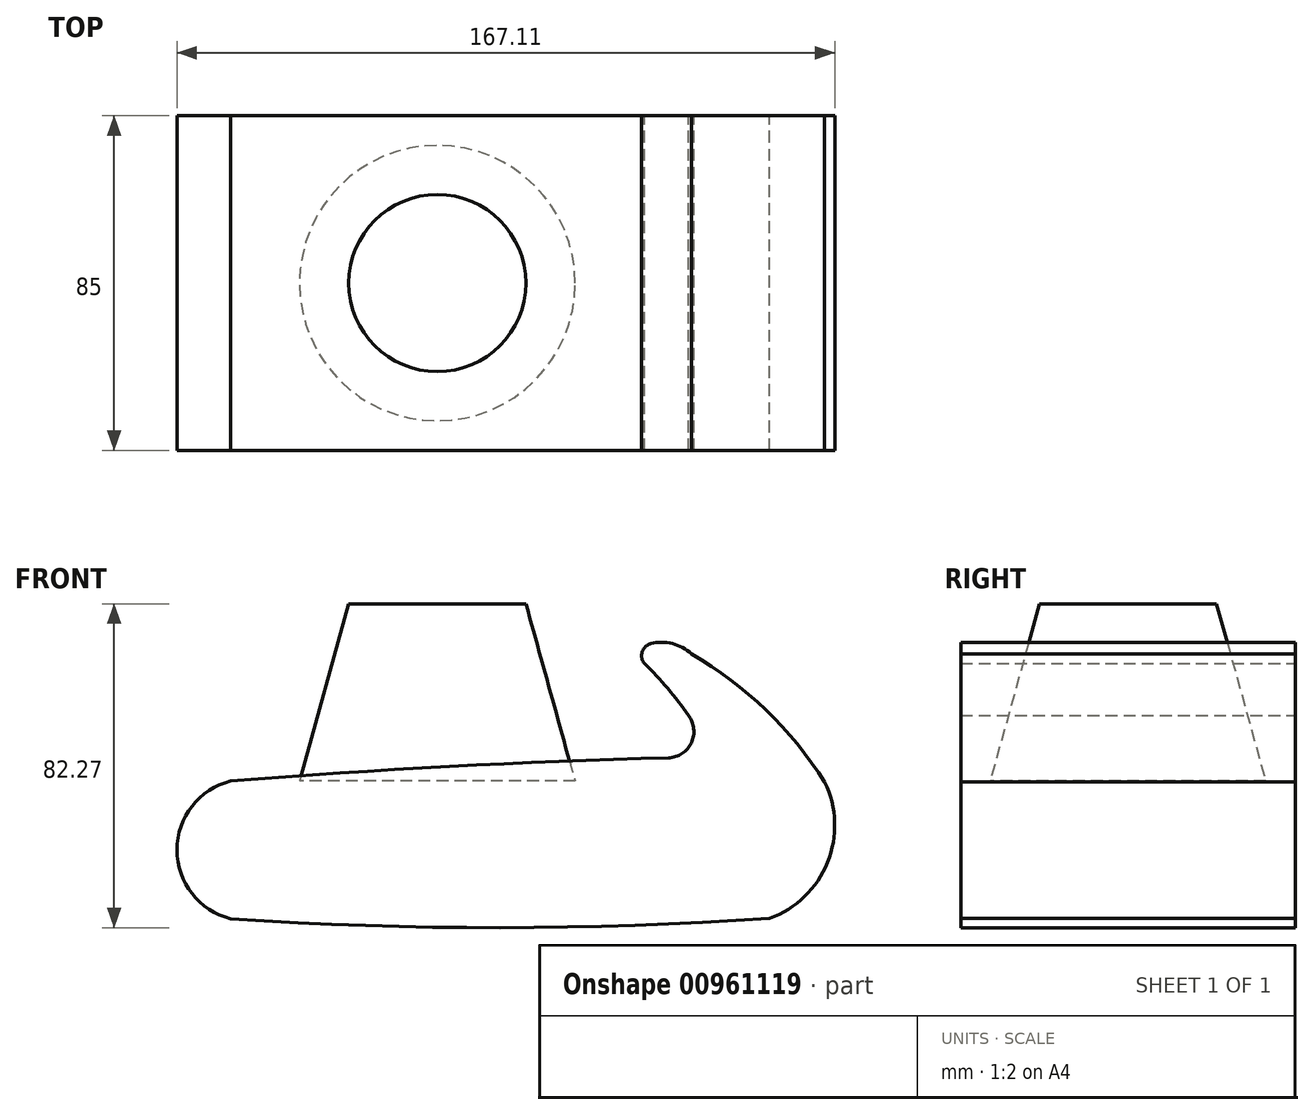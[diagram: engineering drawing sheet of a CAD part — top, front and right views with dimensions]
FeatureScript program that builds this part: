
annotation { "Feature Type Name" : "Feature", "Feature Type Description" : "" }
export const myFeature = defineFeature(function(context is Context, id is Id, definition is map)
    precondition{}
    {
        {
            var Q0;
            Q0=qCreatedBy(makeId("Front.planeOp"),FACE);
            var sketch = newSketch(context, id + "F0", { "sketchPlane" : qUnion([Q0])});
            skLineSegment(sketch, "E0.bottom", {"start": v(52.5, 0) * mm, "end": v(-52.5, 0) * mm, "construction": true});
            skLineSegment(sketch, "E0.top", {"start": v(52.5, 0) * mm, "end": v(-52.5, 0) * mm, "construction": true});
            skLineSegment(sketch, "E0.left", {"start": v(52.5, 0) * mm, "end": v(52.5, 0) * mm});
            skLineSegment(sketch, "E0.right", {"start": v(-52.5, 0) * mm, "end": v(-52.5, 0) * mm});
            skPoint(sketch, "E0.middle", {"position": v(0, 0) * mm});
            skLineSegment(sketch, "E1.bottom", {"start": v(72.5, 0) * mm, "end": v(-72.5, 0) * mm, "construction": true});
            skLineSegment(sketch, "E1.top", {"start": v(72.5, 0) * mm, "end": v(-72.5, 0) * mm, "construction": true});
            skLineSegment(sketch, "E1.left", {"start": v(72.5, 0) * mm, "end": v(72.5, 0) * mm});
            skLineSegment(sketch, "E1.right", {"start": v(-72.5, 0) * mm, "end": v(-72.5, 0) * mm});
            skLineSegment(sketch, "E2.bottom", {"start": v(-52.5, 17.5) * mm, "end": v(-52.5, 17.5) * mm});
            skLineSegment(sketch, "E2.top", {"start": v(-52.5, -17.5) * mm, "end": v(-52.5, -17.5) * mm});
            skLineSegment(sketch, "E2.left", {"start": v(-52.5, 17.5) * mm, "end": v(-52.5, -17.5) * mm, "construction": true});
            skLineSegment(sketch, "E2.right", {"start": v(-52.5, 17.5) * mm, "end": v(-52.5, -17.5) * mm, "construction": true});
            skPoint(sketch, "E2.middle", {"position": v(-52.5, 0) * mm});
            skLineSegment(sketch, "E3.bottom", {"start": v(52.5, 17.5) * mm, "end": v(52.5, 17.5) * mm});
            skLineSegment(sketch, "E3.top", {"start": v(52.5, -17.5) * mm, "end": v(52.5, -17.5) * mm});
            skLineSegment(sketch, "E3.left", {"start": v(52.5, 17.5) * mm, "end": v(52.5, -17.5) * mm, "construction": true});
            skLineSegment(sketch, "E3.right", {"start": v(52.5, 17.5) * mm, "end": v(52.5, -17.5) * mm, "construction": true});
            skPoint(sketch, "E3.middle", {"position": v(52.5, 0) * mm});
            skArc(sketch, "E4", {"start": v(58.7, 23.37) * mm, "mid": v(3.06, 21.19) * mm, "end": v(-52.5, 17.5) * mm});
            skArc(sketch, "E5", {"start": v(58.7, 23.37) * mm, "mid": v(64.55, 27.19) * mm, "end": v(63.77, 34.12) * mm});
            skArc(sketch, "E6", {"start": v(63.77, 34.12) * mm, "mid": v(58.54, 41.01) * mm, "end": v(52.62, 47.31) * mm});
            skArc(sketch, "E7", {"start": v(54.24, 52.38) * mm, "mid": v(52.03, 50.3) * mm, "end": v(52.62, 47.31) * mm});
            skArc(sketch, "E8", {"start": v(64.55, 49.76) * mm, "mid": v(59.74, 52.4) * mm, "end": v(54.24, 52.38) * mm});
            skArc(sketch, "E9", {"start": v(98.4, 17.21) * mm, "mid": v(83.47, 35.56) * mm, "end": v(64.55, 49.76) * mm});
            skArc(sketch, "E10", {"start": v(84.43, -17.4) * mm, "mid": v(99.13, -3.2) * mm, "end": v(98.4, 17.21) * mm});
            skArc(sketch, "E11", {"start": v(-52.5, -17.5) * mm, "mid": v(15.96, -19.77) * mm, "end": v(84.43, -17.4) * mm});
            skArc(sketch, "E12", {"start": v(-52.5, 17.5) * mm, "mid": v(-66.15, 0) * mm, "end": v(-52.5, -17.5) * mm});
            skSolve(sketch);
        }
        {
            var Q0;
            Q0 = qSketchRegion(id + "F0", true);
            extrude(context, id + "F1", {"entities" : qUnion([Q0]), "depth" : 85 * mm, "offsetDistance" : 25 * mm});
        }
        {
            var Q0;
            Q0=qCreatedBy(makeId("Top.planeOp"),FACE);
            cPlane(context, id + "F2", {"entities" : qUnion([Q0]), "cplaneType" : CPlaneType.OFFSET, "offset" : 17.5 * mm, "width" : 150 * mm, "height" : 150 * mm});
        }
        {
            var Q0;
            Q0=qCreatedBy(id+"F2.planeOp",FACE);
            var sketch = newSketch(context, id + "F3", { "sketchPlane" : qUnion([Q0])});
            skLineSegment(sketch, "E13", {"start": v(0, 0) * mm, "end": v(0, -85) * mm, "construction": true});
            skCircle(sketch, "E14", {"center": v(0, -42.5) * mm, "radius": 35 * mm});
            skSolve(sketch);
        }
        {
            var Q0;
            Q0=qCreatedBy(id+"F2.planeOp",FACE);
            cPlane(context, id + "F4", {"entities" : qUnion([Q0]), "cplaneType" : CPlaneType.OFFSET, "offset" : 45 * mm, "width" : 150 * mm, "height" : 150 * mm});
        }
        {
            var Q0;
            Q0=qCreatedBy(id+"F4.planeOp",FACE);
            var sketch = newSketch(context, id + "F5", { "sketchPlane" : qUnion([Q0])});
            skLineSegment(sketch, "E15", {"start": v(0, 0) * mm, "end": v(0, -85) * mm, "construction": true});
            skCircle(sketch, "E16", {"center": v(0, -42.5) * mm, "radius": 22.5 * mm});
            skSolve(sketch);
        }
        {
            var Q0;
            Q0 = qSketchRegion(id + "F3", true);
            var Q1;
            Q1 = qSketchRegion(id + "F5", true);
            var Q2;
            Q2 = qConstructionFilter(qBodyType(qCreatedBy(id + "F3" ,EDGE), BodyType.WIRE), ConstructionObject.NO);
            var Q3;
            Q3 = qConstructionFilter(qBodyType(qCreatedBy(id + "F5" ,EDGE), BodyType.WIRE), ConstructionObject.NO);
            loft(context, id + "F6", {"sheetProfilesArray" : [{ "sheetProfileEntities" : qUnion([Q0]) }, { "sheetProfileEntities" : qUnion([Q1]) }], "wireProfilesArray" : [{ "wireProfileEntities" : qUnion([Q2]) }, { "wireProfileEntities" : qUnion([Q3]) }]});
        }
    });
